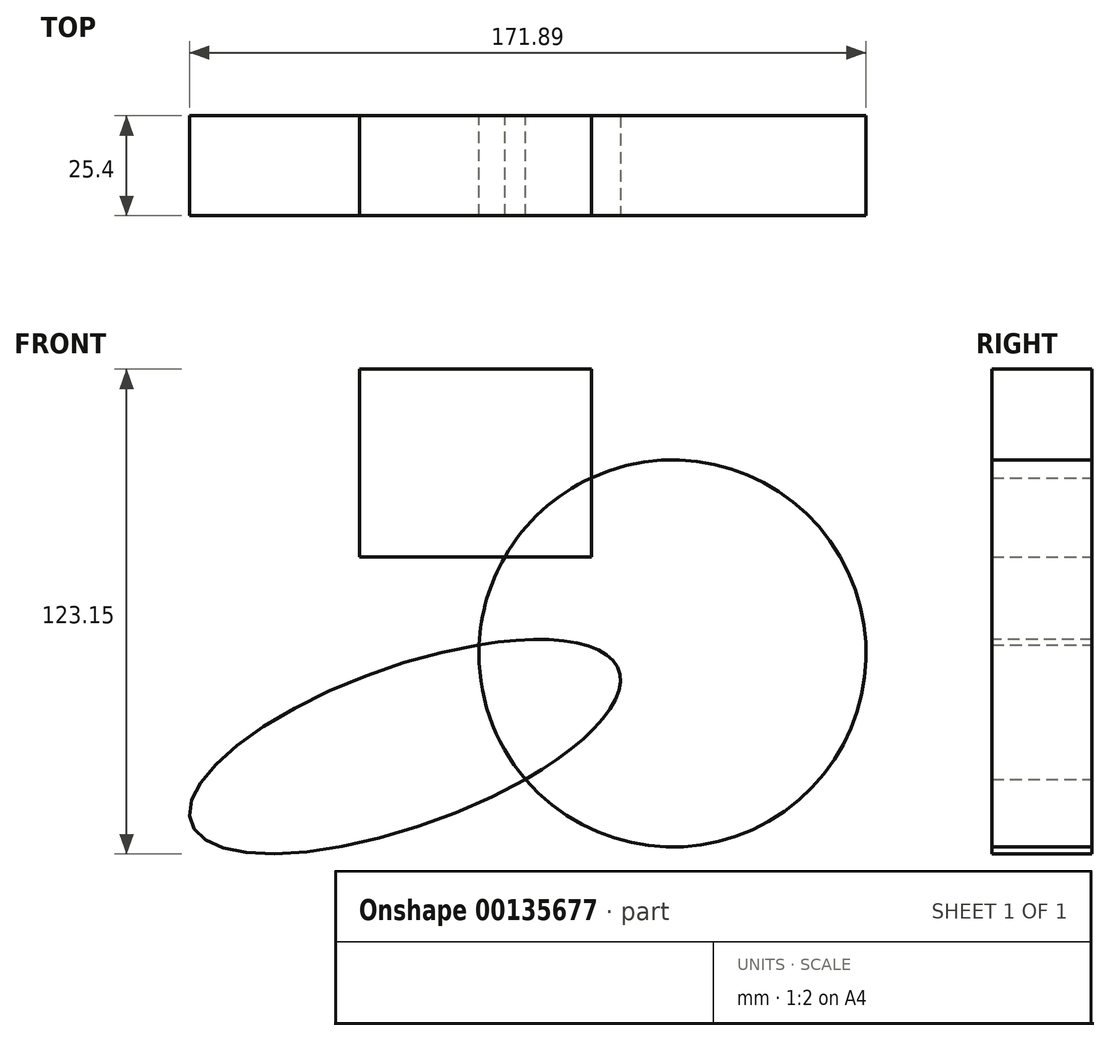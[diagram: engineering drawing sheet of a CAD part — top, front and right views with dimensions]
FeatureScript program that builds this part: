
annotation { "Feature Type Name" : "Feature", "Feature Type Description" : "" }
export const myFeature = defineFeature(function(context is Context, id is Id, definition is map)
    precondition{}
    {
        {
            var Q0;
            Q0=qCreatedBy(makeId("Front.planeOp"),FACE);
            var sketch = newSketch(context, id + "F0", { "sketchPlane" : qUnion([Q0])});
            skLineSegment(sketch, "E0.bottom", {"start": v(-52.23, 6.83) * mm, "end": v(6.68, 6.83) * mm});
            skLineSegment(sketch, "E0.top", {"start": v(-52.23, 54.5) * mm, "end": v(6.68, 54.5) * mm});
            skLineSegment(sketch, "E0.left", {"start": v(-52.23, 6.83) * mm, "end": v(-52.23, 54.5) * mm});
            skLineSegment(sketch, "E0.right", {"start": v(6.68, 6.83) * mm, "end": v(6.68, 54.5) * mm});
            skEllipse(sketch, "E1", {"center": v(-40.7, -41.4) * mm, "majorRadius": 57.67 * mm, "minorRadius": 20.3 * mm, "majorAxis": v(0.94, 0.34)});
            skCircle(sketch, "E2", {"center": v(27.28, -17.74) * mm, "radius": 49.17 * mm});
            skPoint(sketch, "E2.first.point", {"position": v(26.82, 31.43) * mm});
            skPoint(sketch, "E2.second.point", {"position": v(70.85, -40.54) * mm});
            skPoint(sketch, "E2.third.point", {"position": v(64.47, 14.42) * mm});
            skSolve(sketch);
        }
        {
            var Q0;
            {var subQ0=sQuery(id+"F0.wireOp",EDGE,"E2");var subQ1=sQuery(id+"F0.wireOp",EDGE,"E1");var subQ2=makeQuery(id+"F0.imprint","INTERSECT",VERTEX,{"disambiguationData":[OD(0.0)],"derivedFrom":[subQ1,subQ0]});Q0=makeQuery(id+"F0.imprint","IMPRINT",FACE,{"disambiguationData":[TD([[makeQuery(id+"F0.imprint","IMPRINT",EDGE,{"disambiguationData":[TD([[subQ2,-1.0]])],"derivedFrom":subQ1}),1.0]])]});}
            var Q1;
            {var subQ1=sQuery(id+"F0.wireOp",EDGE,"E0.bottom");var subQ6=sQuery(id+"F0.wireOp",EDGE,"E0.right");var subQ7=makeQuery(id+"F0.imprint","INTERSECT",VERTEX,{"derivedFrom":[subQ1,subQ6]});Q1=makeQuery(id+"F0.imprint","IMPRINT",FACE,{"disambiguationData":[TD([[makeQuery(id+"F0.imprint","IMPRINT",EDGE,{"disambiguationData":[TD([[subQ7,1.0]])],"derivedFrom":subQ1}),-1.0]])]});}
            var Q2;
            {var subQ1=sQuery(id+"F0.wireOp",EDGE,"E0.top");Q2=makeQuery(id+"F0.imprint","IMPRINT",FACE,{"disambiguationData":[TD([[makeQuery(id+"F0.imprint","IMPRINT",EDGE,{"derivedFrom":subQ1}),-1.0]])]});}
            extrude(context, id + "F1", {"entities" : qUnion([Q0, Q1, Q2]), "depth" : 25.4 * mm});
        }
    });
